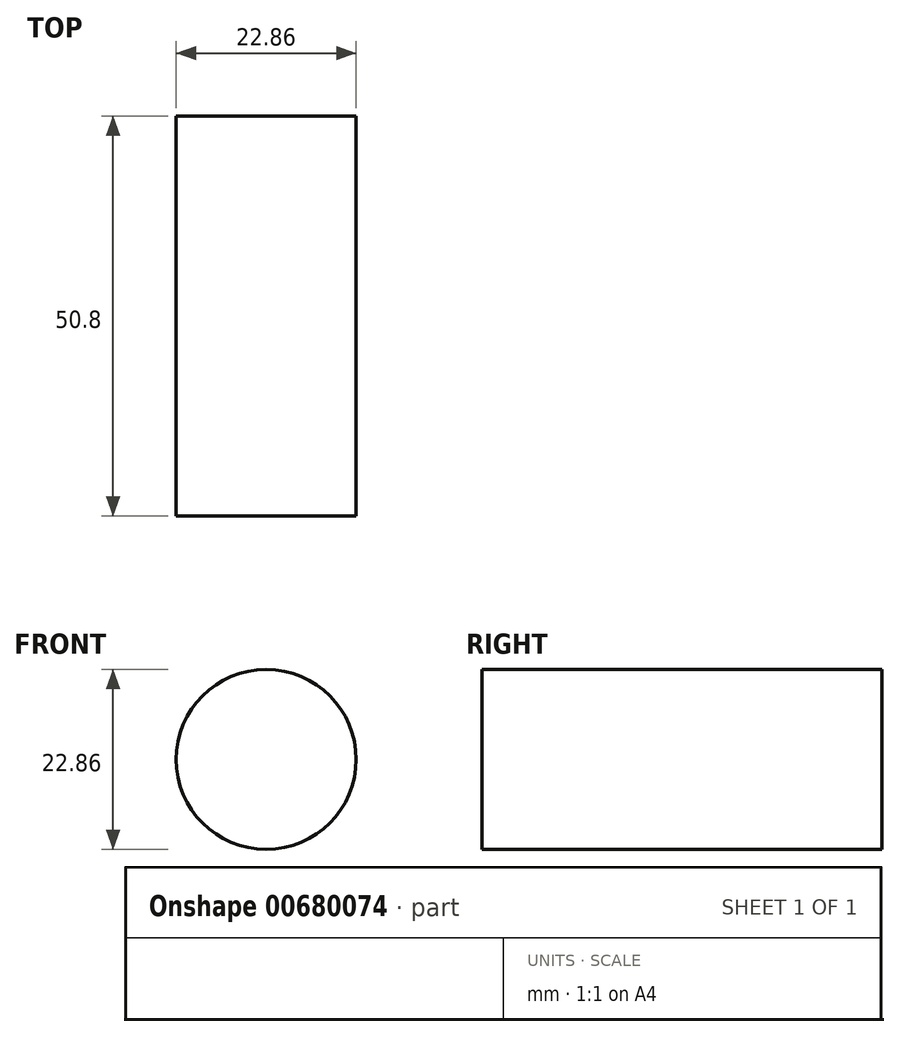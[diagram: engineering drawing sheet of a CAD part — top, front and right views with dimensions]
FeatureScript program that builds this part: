
annotation { "Feature Type Name" : "Feature", "Feature Type Description" : "" }
export const myFeature = defineFeature(function(context is Context, id is Id, definition is map)
    precondition{}
    {
        {
            var Q0;
            Q0=qCreatedBy(makeId("Front.planeOp"),FACE);
            var sketch = newSketch(context, id + "F0", { "sketchPlane" : qUnion([Q0])});
            skCircle(sketch, "E0", {"center": v(0, 0) * mm, "radius": 11.43 * mm});
            skSolve(sketch);
        }
        {
            var Q0;
            Q0=makeQuery(id+"F0.imprint","IMPRINT",FACE,{"disambiguationData":[TD([[makeQuery(id+"F0.imprint","IMPRINT",EDGE,{"derivedFrom":sQuery(id+"F0.wireOp",EDGE,"E0")}),1.0]])]});
            extrude(context, id + "F1", {"entities" : qUnion([Q0]), "depth" : 50.8 * mm, "offsetDistance" : 25.4 * mm});
        }
    });
